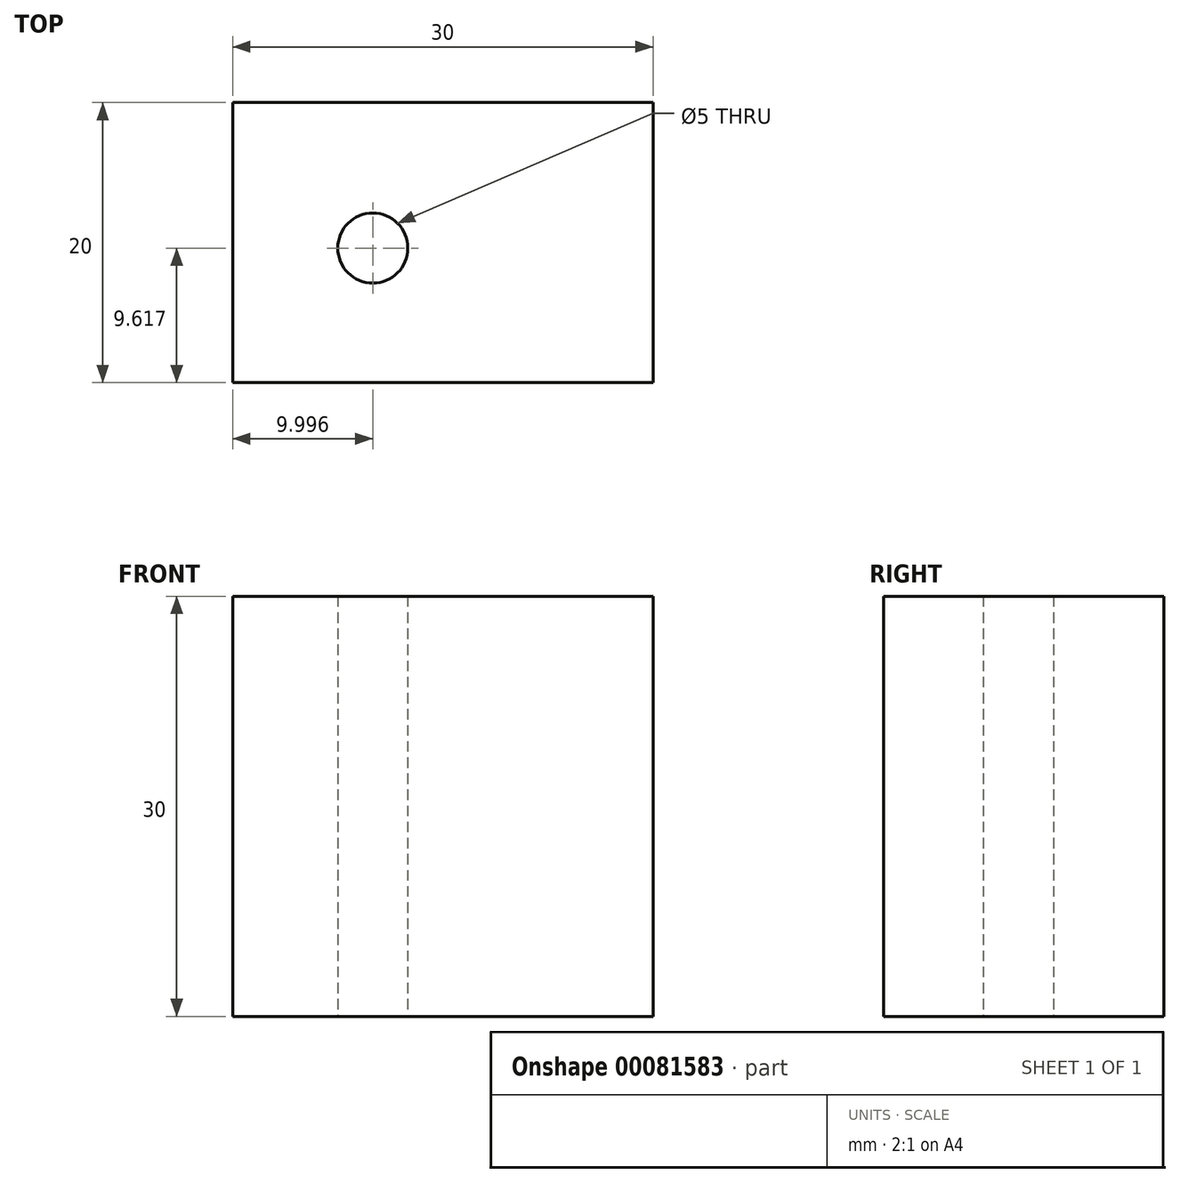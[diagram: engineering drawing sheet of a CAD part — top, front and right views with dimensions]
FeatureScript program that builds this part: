
annotation { "Feature Type Name" : "Feature", "Feature Type Description" : "" }
export const myFeature = defineFeature(function(context is Context, id is Id, definition is map)
    precondition{}
    {
        {
            var Q0;
            Q0=qCreatedBy(makeId("Top.planeOp"),FACE);
            var sketch = newSketch(context, id + "F0", { "sketchPlane" : qUnion([Q0])});
            skLineSegment(sketch, "E0.bottom", {"start": v(-20.71, -26.94) * mm, "end": v(9.29, -26.94) * mm});
            skLineSegment(sketch, "E0.top", {"start": v(-20.71, -6.94) * mm, "end": v(9.29, -6.94) * mm});
            skLineSegment(sketch, "E0.left", {"start": v(-20.71, -26.94) * mm, "end": v(-20.71, -6.94) * mm});
            skLineSegment(sketch, "E0.right", {"start": v(9.29, -26.94) * mm, "end": v(9.29, -6.94) * mm});
            skCircle(sketch, "E1", {"center": v(-10.71, -17.32) * mm, "radius": 2.5 * mm});
            skSolve(sketch);
        }
        {
            var Q0;
            Q0=makeQuery(id+"F0.imprint","IMPRINT",FACE,{"disambiguationData":[TD([[makeQuery(id+"F0.imprint","IMPRINT",EDGE,{"derivedFrom":sQuery(id+"F0.wireOp",EDGE,"E0.bottom")}),1.0]])]});
            extrude(context, id + "F1", {"entities" : qUnion([Q0]), "depth" : 20 * mm, "hasSecondDirection" : true, "secondDirectionOppositeDirection" : true, "secondDirectionDepth" : 10 * mm});
        }
    });
